# Revit family: ergoCentric_airCentric_withoutholesv7
name_source: partatom
category: Generic Models
revit_build: Autodesk Revit 2014 (Build: 20130308_1515(x64)
units: mm (PartAtom-declared; Revit-internal decimal feet)

## types (1)
- ergoCentric_airCentric_withoutholesv7
    Mesh = Steelcase - BR09 Sterling Blue (3D Knit)
    ergoCentric_airCentric_BackSupport01Material = ergoCentric_airCentric_BackSupport01Material
    ergoCentric_airCentric_BackSupport02Material = ergoCentric_airCentric_BackSupport02Material
    ergoCentric_airCentric_BaseMaterial = ergoCentric_airCentric_BaseMaterial
    ergoCentric_airCentric_CasterMaterial = ergoCentric_airCentric_CasterMaterial
    ergoCentric_airCentric_CylinderMaterial = ergoCentric_airCentric_CilynderMaterial
    ergoCentric_airCentric_FrontBarMaterial = ergoCentric_airCentric_FrontBarMaterial
    ergoCentric_airCentric_KnopMaterial = ergoCentric_airCentric_KnopMaterial
    ergoCentric_airCentric_MechanismMaterial = ergoCentric_airCentric_MechanismMaterial
    ergoCentric_airCentric_Peddal02Material = ergoCentric_airCentric_Peddal02Material
    ergoCentric_airCentric_Peddal03Material = ergoCentric_airCentric_Peddal03Material
    ergoCentric_airCentric_Peddal04Material = ergoCentric_airCentric_Peddal04Material
    ergoCentric_airCentric_PeddalMaterial = ergoCentric_airCentric_PeddalMaterial

## geometry (parser evidence)
native form markers: Sweep x46
no freeform markers — native parametric forms only
